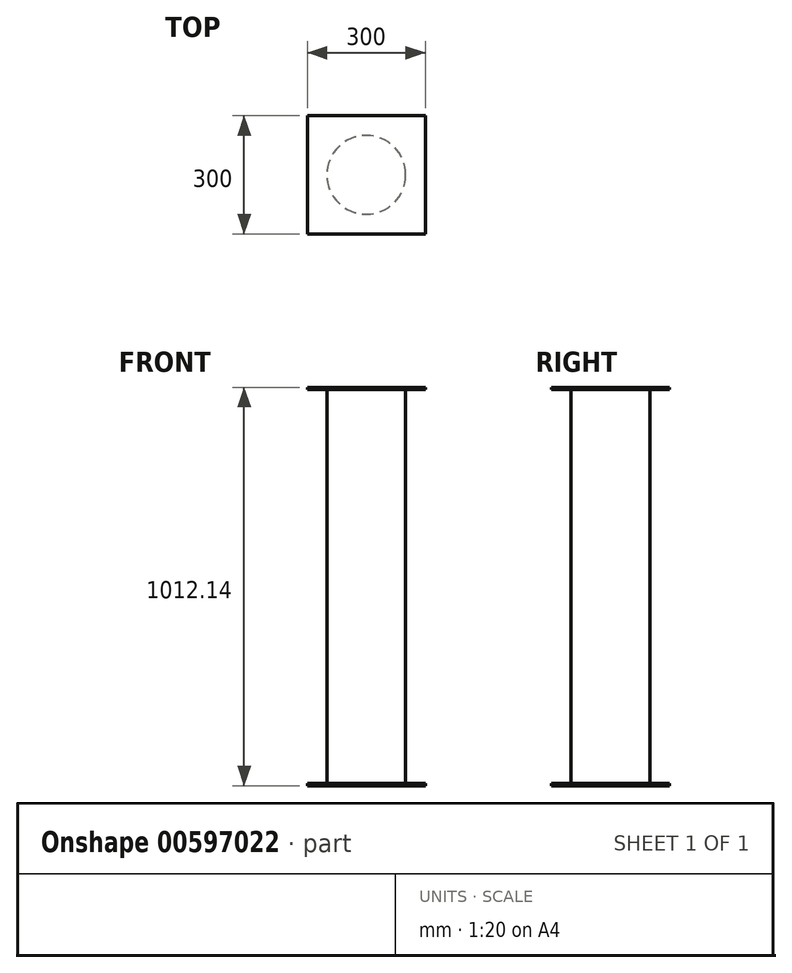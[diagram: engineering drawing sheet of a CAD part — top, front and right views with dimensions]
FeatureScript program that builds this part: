
annotation { "Feature Type Name" : "Feature", "Feature Type Description" : "" }
export const myFeature = defineFeature(function(context is Context, id is Id, definition is map)
    precondition{}
    {
        {
            var Q0;
            Q0=qCreatedBy(makeId("Front.planeOp"),FACE);
            var sketch = newSketch(context, id + "F0", { "sketchPlane" : qUnion([Q0])});
            skLineSegment(sketch, "E0.bottom", {"start": v(150, -3) * mm, "end": v(-150, -3) * mm});
            skLineSegment(sketch, "E0.top", {"start": v(150, 3) * mm, "end": v(-150, 3) * mm});
            skLineSegment(sketch, "E0.left", {"start": v(150, -3) * mm, "end": v(150, 3) * mm});
            skLineSegment(sketch, "E0.right", {"start": v(-150, -3) * mm, "end": v(-150, 3) * mm});
            skPoint(sketch, "E0.middle", {"position": v(0, 0) * mm});
            skSolve(sketch);
        }
        {
            var Q0;
            Q0 = qSketchRegion(id + "F0", true);
            extrude(context, id + "F1", {"entities" : qUnion([Q0]), "endBound" : BoundingType.SYMMETRIC, "depth" : 300 * mm, "offsetDistance" : 25 * mm});
        }
        {
            var Q0;
            Q0=qCreatedBy(makeId("Front.planeOp"),FACE);
            var sketch = newSketch(context, id + "F2", { "sketchPlane" : qUnion([Q0])});
            skLineSegment(sketch, "E1.bottom", {"start": v(0, 3.18) * mm, "end": v(-100, 3.18) * mm});
            skLineSegment(sketch, "E1.top", {"start": v(0, 1003.18) * mm, "end": v(-100, 1003.18) * mm});
            skLineSegment(sketch, "E1.left", {"start": v(0, 3.18) * mm, "end": v(0, 1003.18) * mm});
            skLineSegment(sketch, "E1.right", {"start": v(-100, 3.18) * mm, "end": v(-100, 1003.18) * mm});
            skSolve(sketch);
        }
        {
            var Q0;
            Q0=makeQuery(id+"F2.imprint","IMPRINT",FACE,{"disambiguationData":[TD([[makeQuery(id+"F2.imprint","IMPRINT",EDGE,{"derivedFrom":sQuery(id+"F2.wireOp",EDGE,"E1.bottom")}),-1.0]])]});
            var Q1;
            Q1=sQuery(id+"F2.wireOp",EDGE,"E1.left");
            revolve(context, id + "F3", {"entities" : qUnion([Q0]), "axis" : qUnion([Q1]), "revolveType" : RevolveType.FULL});
        }
        {
            var Q0;
            Q0=makeQuery(id+"F1.opExtrude","SWEPT_BODY",BODY,{"disambiguationData":[OSD([sQuery(id+"F0.wireOp",EDGE,"E0.bottom"),sQuery(id+"F0.wireOp",EDGE,"E0.top"),sQuery(id+"F0.wireOp",EDGE,"E0.left"),sQuery(id+"F0.wireOp",EDGE,"E0.right")])]});
            transform(context, id + "F4", {"entities" : qUnion([Q0]), "transformType" : TransformType.TRANSLATION_3D, "dx" : 0 * mm, "dy" : 0 * mm, "dz" : 0 * mm, "makeCopy" : true});
        }
        {
            var Q0;
            Q0=qCreatedBy(makeId("Front.planeOp"),FACE);
            var sketch = newSketch(context, id + "F5", { "sketchPlane" : qUnion([Q0])});
            skLineSegment(sketch, "E2.bottom", {"start": v(150, 1003.14) * mm, "end": v(-150, 1003.14) * mm});
            skLineSegment(sketch, "E2.top", {"start": v(150, 1009.14) * mm, "end": v(-150, 1009.14) * mm});
            skLineSegment(sketch, "E2.left", {"start": v(150, 1003.14) * mm, "end": v(150, 1009.14) * mm});
            skLineSegment(sketch, "E2.right", {"start": v(-150, 1003.14) * mm, "end": v(-150, 1009.14) * mm});
            skPoint(sketch, "E2.middle", {"position": v(0, 1006.14) * mm});
            skSolve(sketch);
        }
        {
            var Q0;
            Q0=makeQuery(id+"F5.imprint","IMPRINT",FACE,{"disambiguationData":[TD([[makeQuery(id+"F5.imprint","IMPRINT",EDGE,{"derivedFrom":sQuery(id+"F5.wireOp",EDGE,"E2.bottom")}),-1.0]])]});
            extrude(context, id + "F6", {"entities" : qUnion([Q0]), "operationType" : NewBodyOperationType.ADD, "endBound" : BoundingType.SYMMETRIC, "depth" : 300 * mm, "offsetDistance" : 25 * mm});
        }
    });
